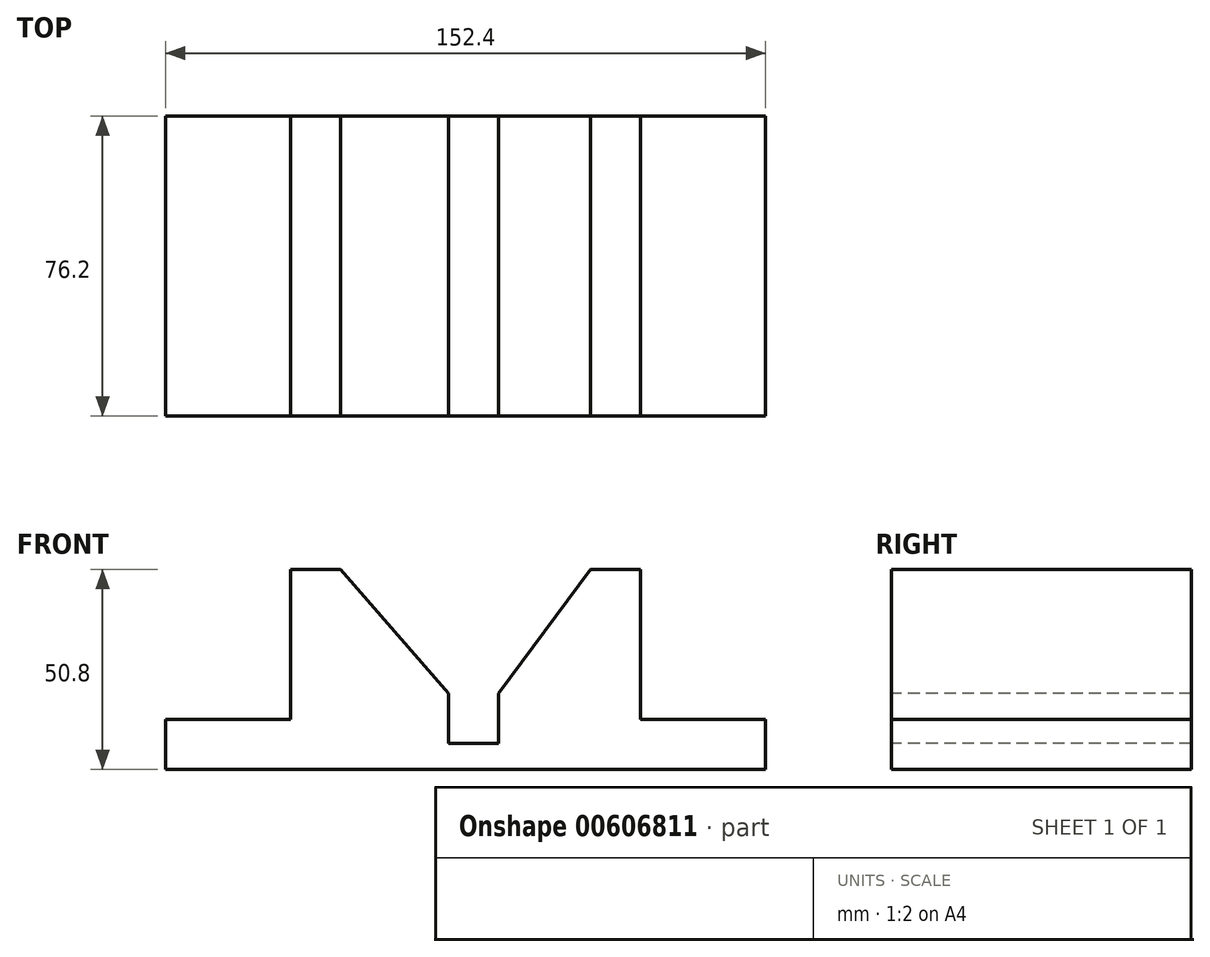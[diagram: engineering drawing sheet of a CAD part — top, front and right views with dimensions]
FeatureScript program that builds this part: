
annotation { "Feature Type Name" : "Feature", "Feature Type Description" : "" }
export const myFeature = defineFeature(function(context is Context, id is Id, definition is map)
    precondition{}
    {
        {
            var Q0;
            Q0=qCreatedBy(makeId("Front.planeOp"),FACE);
            var sketch = newSketch(context, id + "F0", { "sketchPlane" : qUnion([Q0])});
            skLineSegment(sketch, "E0", {"start": v(0, 0) * mm, "end": v(152.4, 0) * mm});
            skLineSegment(sketch, "E1", {"start": v(152.4, 0) * mm, "end": v(152.4, 12.7) * mm});
            skLineSegment(sketch, "E2", {"start": v(152.4, 12.7) * mm, "end": v(120.65, 12.7) * mm});
            skLineSegment(sketch, "E3", {"start": v(120.65, 12.7) * mm, "end": v(120.65, 50.8) * mm});
            skLineSegment(sketch, "E4", {"start": v(120.65, 50.8) * mm, "end": v(107.95, 50.8) * mm});
            skLineSegment(sketch, "E5", {"start": v(107.95, 50.8) * mm, "end": v(84.56, 19.35) * mm});
            skLineSegment(sketch, "E6", {"start": v(84.56, 19.35) * mm, "end": v(84.56, 6.65) * mm});
            skLineSegment(sketch, "E7", {"start": v(84.56, 6.65) * mm, "end": v(71.86, 6.65) * mm});
            skLineSegment(sketch, "E8", {"start": v(71.86, 6.65) * mm, "end": v(71.86, 19.35) * mm});
            skLineSegment(sketch, "E9", {"start": v(71.86, 19.35) * mm, "end": v(44.45, 50.8) * mm});
            skLineSegment(sketch, "E10", {"start": v(44.45, 50.8) * mm, "end": v(31.75, 50.8) * mm});
            skLineSegment(sketch, "E11", {"start": v(31.75, 50.8) * mm, "end": v(31.75, 12.7) * mm});
            skLineSegment(sketch, "E12", {"start": v(31.75, 12.7) * mm, "end": v(0, 12.7) * mm});
            skLineSegment(sketch, "E13", {"start": v(0, 12.7) * mm, "end": v(0, 0) * mm});
            skSolve(sketch);
        }
        {
            var Q0;
            Q0=makeQuery(id+"F0.imprint","IMPRINT",FACE,{"disambiguationData":[TD([[makeQuery(id+"F0.imprint","IMPRINT",EDGE,{"derivedFrom":sQuery(id+"F0.wireOp",EDGE,"E0")}),1.0]])]});
            extrude(context, id + "F1", {"entities" : qUnion([Q0]), "oppositeDirection" : true, "depth" : 76.2 * mm, "offsetDistance" : 25.4 * mm});
        }
    });
